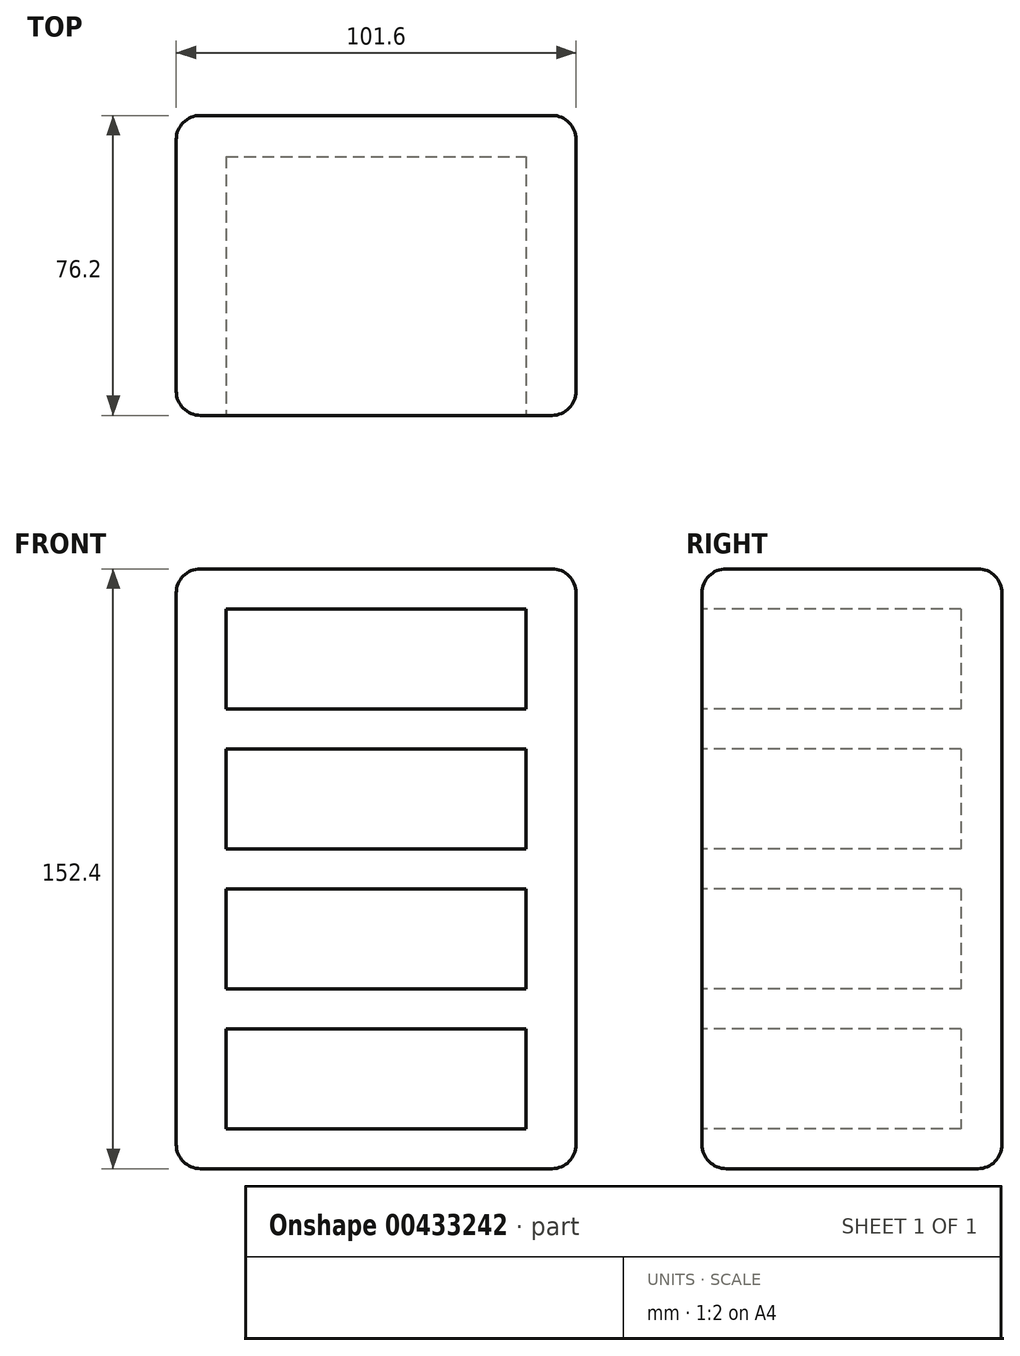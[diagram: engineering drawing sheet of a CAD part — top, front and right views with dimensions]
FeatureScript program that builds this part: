
annotation { "Feature Type Name" : "Feature", "Feature Type Description" : "" }
export const myFeature = defineFeature(function(context is Context, id is Id, definition is map)
    precondition{}
    {
        {
            var Q0;
            Q0=qCreatedBy(makeId("Top.planeOp"),FACE);
            var sketch = newSketch(context, id + "F0", { "sketchPlane" : qUnion([Q0])});
            skLineSegment(sketch, "E0.bottom", {"start": v(-60.89, -36.09) * mm, "end": v(40.71, -36.09) * mm});
            skLineSegment(sketch, "E0.top", {"start": v(-60.89, 40.11) * mm, "end": v(40.71, 40.11) * mm});
            skLineSegment(sketch, "E0.left", {"start": v(-60.89, -36.09) * mm, "end": v(-60.89, 40.11) * mm});
            skLineSegment(sketch, "E0.right", {"start": v(40.71, -36.09) * mm, "end": v(40.71, 40.11) * mm});
            skSolve(sketch);
        }
        {
            var Q0;
            Q0=makeQuery(id+"F0.imprint","IMPRINT",FACE,{"disambiguationData":[TD([[makeQuery(id+"F0.imprint","IMPRINT",EDGE,{"derivedFrom":sQuery(id+"F0.wireOp",EDGE,"E0.bottom")}),1.0]])]});
            extrude(context, id + "F1", {"entities" : qUnion([Q0]), "depth" : 152.4 * mm});
        }
        {
            var Q0;
            Q0=makeQuery(id+"F1.opExtrude","SWEPT_FACE",FACE,{"disambiguationData":[OSD([sQuery(id+"F0.wireOp",EDGE,"E0.bottom")])]});
            var sketch = newSketch(context, id + "F2", { "sketchPlane" : qUnion([Q0])});
            skLineSegment(sketch, "E1.bottom", {"start": v(-48.19, 142.24) * mm, "end": v(28.01, 142.24) * mm});
            skLineSegment(sketch, "E1.top", {"start": v(-48.19, 116.84) * mm, "end": v(28.01, 116.84) * mm});
            skLineSegment(sketch, "E1.left", {"start": v(-48.19, 142.24) * mm, "end": v(-48.19, 116.84) * mm});
            skLineSegment(sketch, "E1.right", {"start": v(28.01, 142.24) * mm, "end": v(28.01, 116.84) * mm});
            skLineSegment(sketch, "E2.0.1.0", {"start": v(-48.19, 106.68) * mm, "end": v(-48.19, 81.28) * mm});
            skLineSegment(sketch, "E2.0.1.1", {"start": v(-48.19, 106.68) * mm, "end": v(28.01, 106.68) * mm});
            skLineSegment(sketch, "E2.0.1.2", {"start": v(28.01, 106.68) * mm, "end": v(28.01, 81.28) * mm});
            skLineSegment(sketch, "E2.0.1.3", {"start": v(-48.19, 81.28) * mm, "end": v(28.01, 81.28) * mm});
            skLineSegment(sketch, "E2.0.2.0", {"start": v(-48.19, 71.12) * mm, "end": v(-48.19, 45.72) * mm});
            skLineSegment(sketch, "E2.0.2.1", {"start": v(-48.19, 71.12) * mm, "end": v(28.01, 71.12) * mm});
            skLineSegment(sketch, "E2.0.2.2", {"start": v(28.01, 71.12) * mm, "end": v(28.01, 45.72) * mm});
            skLineSegment(sketch, "E2.0.2.3", {"start": v(-48.19, 45.72) * mm, "end": v(28.01, 45.72) * mm});
            skLineSegment(sketch, "E2.0.3.0", {"start": v(-48.19, 35.56) * mm, "end": v(-48.19, 10.16) * mm});
            skLineSegment(sketch, "E2.0.3.1", {"start": v(-48.19, 35.56) * mm, "end": v(28.01, 35.56) * mm});
            skLineSegment(sketch, "E2.0.3.2", {"start": v(28.01, 35.56) * mm, "end": v(28.01, 10.16) * mm});
            skLineSegment(sketch, "E2.0.3.3", {"start": v(-48.19, 10.16) * mm, "end": v(28.01, 10.16) * mm});
            skLineSegment(sketch, "E2.direction1", {"start": v(-48.19, 116.84) * mm, "end": v(-22.79, 116.84) * mm, "construction": true});
            skLineSegment(sketch, "E2.direction2", {"start": v(-48.19, 116.84) * mm, "end": v(-48.19, 81.28) * mm, "construction": true});
            skSolve(sketch);
        }
        {
            var Q0;
            Q0=makeQuery(id+"F2.imprint","IMPRINT",FACE,{"disambiguationData":[TD([[makeQuery(id+"F2.imprint","IMPRINT",EDGE,{"derivedFrom":sQuery(id+"F2.wireOp",EDGE,"E1.bottom")}),-1.0]])]});
            var Q1;
            Q1=makeQuery(id+"F2.imprint","IMPRINT",FACE,{"disambiguationData":[TD([[makeQuery(id+"F2.imprint","IMPRINT",EDGE,{"derivedFrom":sQuery(id+"F2.wireOp",EDGE,"E2.0.1.0")}),1.0]])]});
            var Q2;
            Q2=makeQuery(id+"F2.imprint","IMPRINT",FACE,{"disambiguationData":[TD([[makeQuery(id+"F2.imprint","IMPRINT",EDGE,{"derivedFrom":sQuery(id+"F2.wireOp",EDGE,"E2.0.2.0")}),1.0]])]});
            var Q3;
            Q3=makeQuery(id+"F2.imprint","IMPRINT",FACE,{"disambiguationData":[TD([[makeQuery(id+"F2.imprint","IMPRINT",EDGE,{"derivedFrom":sQuery(id+"F2.wireOp",EDGE,"E2.0.3.0")}),1.0]])]});
            extrude(context, id + "F3", {"entities" : qUnion([Q0, Q1, Q2, Q3]), "operationType" : NewBodyOperationType.REMOVE, "oppositeDirection" : true, "depth" : 65.8 * mm});
        }
        {
            var Q0;
            Q0=makeQuery(id+"F1.opExtrude","CAP_EDGE",EDGE,{"disambiguationData":[OSD([sQuery(id+"F0.wireOp",EDGE,"E0.left")])],"isStart":false});
            var Q1;
            Q1=makeQuery(id+"F1.opExtrude","CAP_EDGE",EDGE,{"disambiguationData":[OSD([sQuery(id+"F0.wireOp",EDGE,"E0.bottom")])],"isStart":false});
            var Q2;
            Q2=makeQuery(id+"F1.opExtrude","CAP_EDGE",EDGE,{"disambiguationData":[OSD([sQuery(id+"F0.wireOp",EDGE,"E0.right")])],"isStart":false});
            var Q3;
            Q3=makeQuery(id+"F1.opExtrude","CAP_EDGE",EDGE,{"disambiguationData":[OSD([sQuery(id+"F0.wireOp",EDGE,"E0.top")])],"isStart":false});
            var Q4;
            Q4=makeQuery(id+"F1.opExtrude","SWEPT_EDGE",EDGE,{"disambiguationData":[OSD([sQuery(id+"F0.wireOp",EDGE,"E0.bottom"),sQuery(id+"F0.wireOp",EDGE,"E0.right")])]});
            var Q5;
            Q5=makeQuery(id+"F1.opExtrude","SWEPT_EDGE",EDGE,{"disambiguationData":[OSD([sQuery(id+"F0.wireOp",EDGE,"E0.top"),sQuery(id+"F0.wireOp",EDGE,"E0.right")])]});
            var Q6;
            Q6=makeQuery(id+"F1.opExtrude","SWEPT_EDGE",EDGE,{"disambiguationData":[OSD([sQuery(id+"F0.wireOp",EDGE,"E0.top"),sQuery(id+"F0.wireOp",EDGE,"E0.left")])]});
            var Q7;
            Q7=makeQuery(id+"F1.opExtrude","SWEPT_EDGE",EDGE,{"disambiguationData":[OSD([sQuery(id+"F0.wireOp",EDGE,"E0.bottom"),sQuery(id+"F0.wireOp",EDGE,"E0.left")])]});
            var Q8;
            Q8=makeQuery(id+"F1.opExtrude","CAP_EDGE",EDGE,{"disambiguationData":[OSD([sQuery(id+"F0.wireOp",EDGE,"E0.bottom")])],"isStart":true});
            var Q9;
            Q9=makeQuery(id+"F1.opExtrude","CAP_EDGE",EDGE,{"disambiguationData":[OSD([sQuery(id+"F0.wireOp",EDGE,"E0.top")])],"isStart":true});
            var Q10;
            Q10=makeQuery(id+"F1.opExtrude","CAP_EDGE",EDGE,{"disambiguationData":[OSD([sQuery(id+"F0.wireOp",EDGE,"E0.right")])],"isStart":true});
            var Q11;
            Q11=makeQuery(id+"F1.opExtrude","CAP_EDGE",EDGE,{"disambiguationData":[OSD([sQuery(id+"F0.wireOp",EDGE,"E0.left")])],"isStart":true});
            fillet(context, id + "F4", {"entities" : qUnion([Q0, Q1, Q2, Q3, Q4, Q5, Q6, Q7, Q8, Q9, Q10, Q11]), "radius" : 6.13 * mm, "tangentPropagation" : true, "allowEdgeOverflow" : false});
        }
    });
